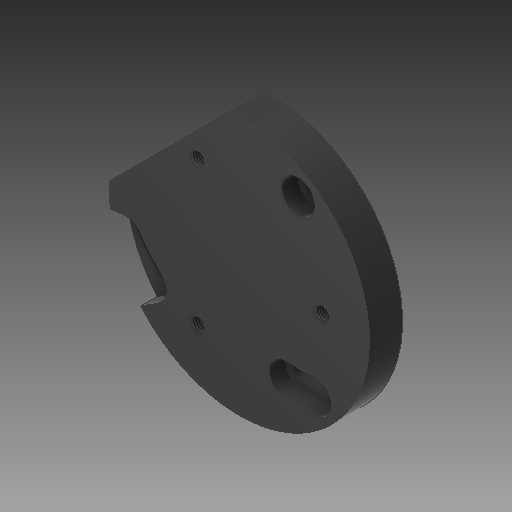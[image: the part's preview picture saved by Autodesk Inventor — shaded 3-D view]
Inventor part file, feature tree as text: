
AUTODESK INVENTOR PART (.ipt)
format: ipt  version: 2018 (Build 220112000, 112)  size: 221,696 bytes
history: native  units: in
note: dims shown in document units (in); Inventor stores cm internally (conversion verified against a paired STEP export)
features: extrude x12, sketch x8, thread x3
ambient origin geometry x8: Origin, YZ Plane, XZ Plane, XY Plane, X Axis, Y Axis, Z Axis, Center Point
bodies: Solid1 (feature_tree)
feature tree (23):
  extrude  "Extrusion1"  Depth=0.2362in
  sketch  "Sketch2"  dims[d9=0.2362in d10=0.2362in]
  extrude  "Extrusion2"  Depth=0.2362in
  extrude  "Extrusion3"  Depth=0.3937in
  extrude  "Extrusion4"  Depth=0.3937in
  sketch  "Sketch3"  dims[d11=0.3937in d12=0.0in d13=0.3937in]
  extrude  "Extrusion5"  Depth=0.1969in TaperAngle=0.0deg
  extrude  "Extrusion6"  Depth=0.1969in
  extrude  "Extrusion7"  Depth=0.3937in TaperAngle=0.0deg
  sketch  "Sketch5"  dims[d14=0.3937in d15=0.3937in]
  extrude  "Extrusion11"  Depth=0.3937in TaperAngle=0.0deg
  sketch  "Sketch6"  dims[d16=0.1969in d17=0.0in d18=0.1969in d19=0.0in]
  extrude  "Extrusion14"  Depth=0.3937in
  extrude  "Extrusion15"  Depth=0.1969in TaperAngle=0.0deg
  extrude  "Extrusion16"  Depth=0.3937in
  extrude  "Extrusion17"  Depth=0.3937in
  thread  "Thread1"  [1 undecoded]
  thread  "Thread2"  [1 undecoded]
  thread  "Thread3"  [1 undecoded]
  sketch  "Sketch1"  dims[d0=3.0906in d6=0.2362in]
  sketch  "Sketch7"  dims[d20=0.1969in d21=0.0in d24=0.1575in]
  sketch  "Sketch8"  dims[d25=1.1811in d27=360.0deg d29=0.3937in d30=0.0in]
  sketch  "Sketch9"  dims[d31=0.3937in d32=0.0in d33=0.3937in d34=0.0in d57=0.3937in d62=0.1969in d63=0.0in d69=4.1732in d70=0.2362in d71=0.2362in d74=0.1969in d75=0.0in d77=135.0deg d78=0.3937in d79=0.0in d84=0.3937in d87=0.3937in d88=0.1969in d89=0.0in d90=0.2362in d92=0.2362in d93=0.1969in d94=0.0in d95=0.3937in d96=0.0in d97=0.3937in d98=0.0in d99=0.3937in d100=0.0in]
note: 3 required parameter values undecoded (feature->parameter linkage not recoverable at this tier; creation-order binding heuristic only, values carry confidence <= 0.55)
